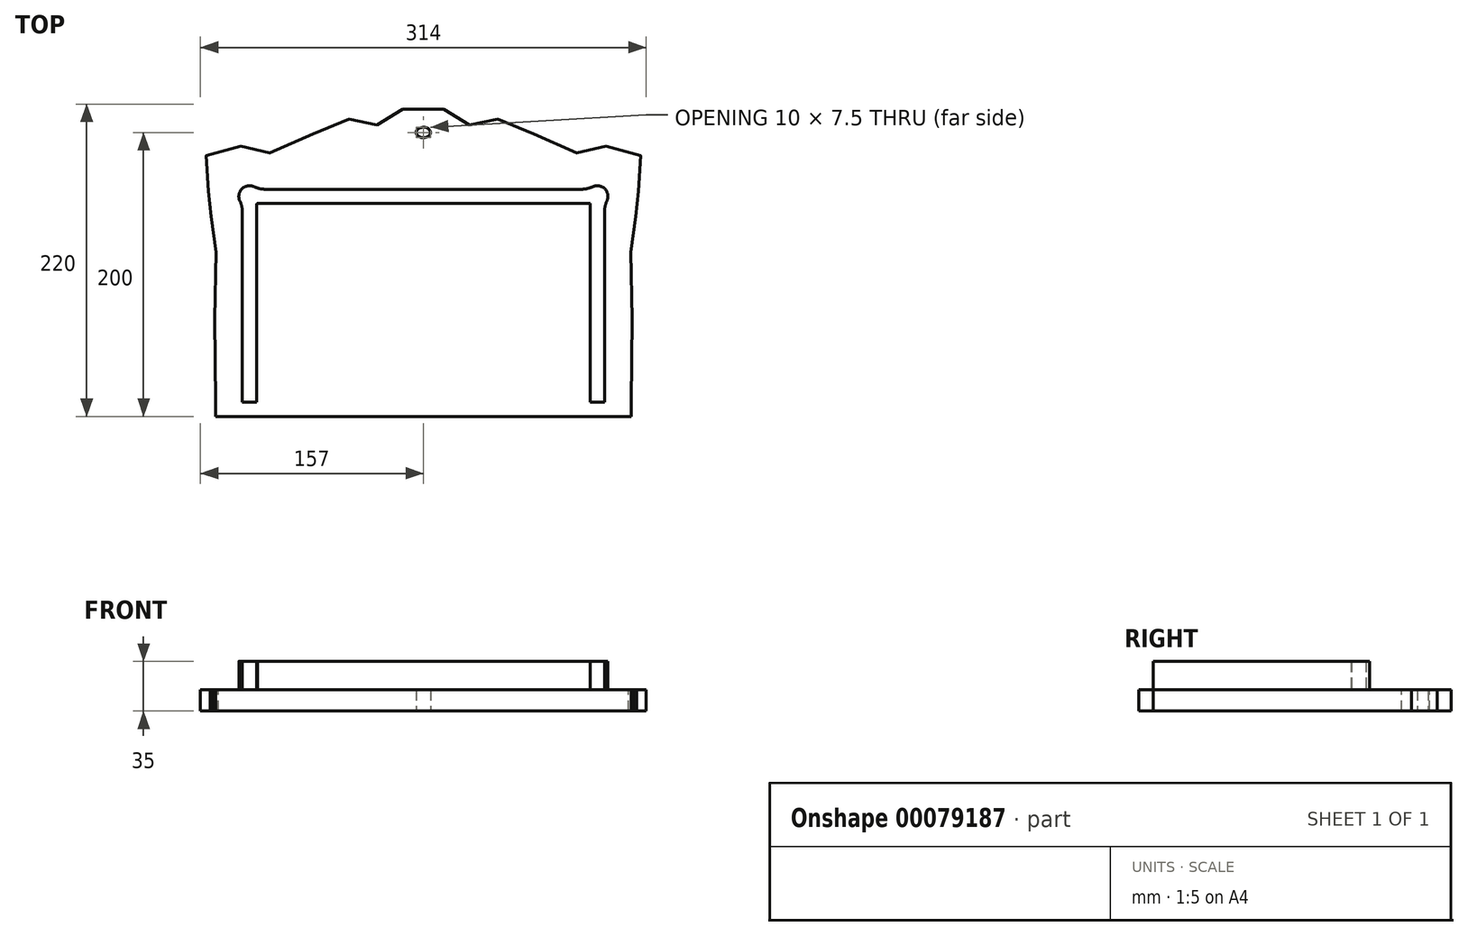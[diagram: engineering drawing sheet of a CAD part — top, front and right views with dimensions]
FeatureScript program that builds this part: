
annotation { "Feature Type Name" : "Feature", "Feature Type Description" : "" }
export const myFeature = defineFeature(function(context is Context, id is Id, definition is map)
    precondition{}
    {
        {
            var Q0;
            Q0=qCreatedBy(makeId("Top.planeOp"),FACE);
            var sketch = newSketch(context, id + "F0", { "sketchPlane" : qUnion([Q0])});
            skPoint(sketch, "E0", {"position": v(151.1, 154.93) * mm});
            skPoint(sketch, "E1", {"position": v(140, 77.47) * mm});
            skPoint(sketch, "E2", {"position": v(146.5, 0) * mm});
            skPoint(sketch, "E3", {"position": v(0, 210) * mm});
            skPoint(sketch, "E4", {"position": v(72.86, 179.48) * mm});
            skPoint(sketch, "E5", {"position": v(-38.35, 186.04) * mm});
            skPoint(sketch, "E6", {"position": v(-24.12, 200) * mm});
            skPoint(sketch, "E7", {"position": v(-154.5, 163.42) * mm});
            skLineSegment(sketch, "E8", {"start": v(0, 210) * mm, "end": v(0, -300) * mm, "construction": true});
            skPoint(sketch, "E9.MirrorP", {"position": v(-72.86, 179.48) * mm});
            skPoint(sketch, "E10.MirrorP", {"position": v(-151.1, 154.93) * mm});
            skPoint(sketch, "E11.MirrorP", {"position": v(-140, 77.47) * mm});
            skPoint(sketch, "E12.MirrorP", {"position": v(-146.5, 0) * mm});
            skPoint(sketch, "E13", {"position": v(0, 0) * mm});
            skPoint(sketch, "E14.MirrorP", {"position": v(154.5, 163.42) * mm});
            skPoint(sketch, "E15.MirrorP", {"position": v(38.35, 186.04) * mm});
            skPoint(sketch, "E16.MirrorP", {"position": v(24.12, 200) * mm});
            skPoint(sketch, "E17", {"position": v(-111.22, 185.44) * mm});
            skPoint(sketch, "E18.MirrorP", {"position": v(111.21, 185.44) * mm});
            skLineSegment(sketch, "E19", {"start": v(-146.5, 0) * mm, "end": v(146.5, 0) * mm});
            skPoint(sketch, "E20", {"position": v(0, 193.84) * mm});
            skPoint(sketch, "E21", {"position": v(-120.16, 190.34) * mm});
            skPoint(sketch, "E22", {"position": v(-131.3, 192.59) * mm});
            skPoint(sketch, "E23", {"position": v(-143.04, 189.12) * mm});
            skPoint(sketch, "E24", {"position": v(-150.16, 182.65) * mm});
            skPoint(sketch, "E25", {"position": v(-153.61, 176.08) * mm});
            skPoint(sketch, "E26", {"position": v(-154.92, 169.2) * mm});
            skPoint(sketch, "E27.MirrorP", {"position": v(120.16, 190.34) * mm});
            skPoint(sketch, "E28.MirrorP", {"position": v(131.3, 192.59) * mm});
            skPoint(sketch, "E29.MirrorP", {"position": v(143.04, 189.12) * mm});
            skPoint(sketch, "E30.MirrorP", {"position": v(150.16, 182.65) * mm});
            skPoint(sketch, "E31.MirrorP", {"position": v(153.61, 176.08) * mm});
            skPoint(sketch, "E32.MirrorP", {"position": v(154.92, 169.2) * mm});
            skFitSpline(sketch, "E33", {"points": [v(-146.5, 0) * mm, v(-140, 77.47) * mm, v(-151.1, 154.93) * mm, v(-154.5, 163.42) * mm, v(-154.92, 169.2) * mm, v(-153.61, 176.08) * mm, v(-150.16, 182.65) * mm, v(-143.04, 189.12) * mm, v(-131.3, 192.59) * mm, v(-120.16, 190.34) * mm, v(-111.22, 185.44) * mm, v(-72.87, 179.48) * mm, v(-38.35, 186.04) * mm, v(-24.12, 200) * mm, v(0, 210) * mm, v(24.12, 200) * mm, v(38.35, 186.04) * mm, v(72.86, 179.48) * mm, v(111.21, 185.44) * mm, v(120.16, 190.34) * mm, v(131.3, 192.59) * mm, v(143.04, 189.12) * mm, v(150.16, 182.65) * mm, v(153.61, 176.08) * mm, v(154.92, 169.2) * mm, v(154.5, 163.42) * mm, v(151.1, 154.93) * mm, v(140, 77.47) * mm, v(146.5, 0) * mm], "startDerivative": vector(163.85, 1049.48) * mm, "endDerivative": vector(163.85, -1049.48) * mm});
            skLineSegment(sketch, "E34.bottom", {"start": v(-107.5, 0) * mm, "end": v(107.5, 0) * mm});
            skSolve(sketch);
        }
        {
            var Q0;
            Q0=qCreatedBy(makeId("Top.planeOp"),FACE);
            cPlane(context, id + "F1", {"entities" : qUnion([Q0]), "cplaneType" : CPlaneType.OFFSET, "offset" : 100 * mm, "width" : 150 * mm, "height" : 150 * mm});
        }
        {
            var Q0;
            Q0=qCreatedBy(id+"F1.planeOp",FACE);
            var sketch = newSketch(context, id + "F2", { "sketchPlane" : qUnion([Q0])});
            skPoint(sketch, "E35.0", {"position": v(-146.5, 0) * mm});
            skPoint(sketch, "E36", {"position": v(-150, 128) * mm});
            skPoint(sketch, "E37", {"position": v(-15, 206) * mm});
            skPoint(sketch, "E38", {"position": v(-83.69, 186) * mm});
            skPoint(sketch, "E39", {"position": v(-57.22, 198) * mm});
            skPoint(sketch, "E40.16.internal.orphan", {"position": v(-102.04, 177) * mm});
            skPoint(sketch, "E40.2.internal.orphan", {"position": v(-147, 60) * mm});
            skLineSegment(sketch, "E41", {"start": v(-146.5, 0) * mm, "end": v(146.5, 0) * mm});
            skLineSegment(sketch, "E42", {"start": v(0, 0) * mm, "end": v(0, 210) * mm, "construction": true});
            skPoint(sketch, "E42.endSnap0", {"position": v(0, 0) * mm});
            skLineSegment(sketch, "E43", {"start": v(214.08, 0) * mm, "end": v(-299.05, 0) * mm, "construction": true});
            skPoint(sketch, "E44.10.internal.orphan", {"position": v(-151, 176) * mm});
            skPoint(sketch, "E44.11.internal.orphan", {"position": v(-138, 182) * mm});
            skPoint(sketch, "E44.12.internal.orphan", {"position": v(-116, 175) * mm});
            skPoint(sketch, "E44.15.internal.orphan", {"position": v(-67.88, 193.66) * mm});
            skPoint(sketch, "E44.17.internal.orphan", {"position": v(-46.27, 200) * mm});
            skPoint(sketch, "E44.18.internal.orphan", {"position": v(-38.42, 198) * mm});
            skPoint(sketch, "E44.19.internal.orphan", {"position": v(-34.04, 196) * mm});
            skPoint(sketch, "E44.2.internal.orphan", {"position": v(-145, 100) * mm});
            skPoint(sketch, "E44.20.internal.orphan", {"position": v(-29, 195) * mm});
            skPoint(sketch, "E44.21.internal.orphan", {"position": v(-25, 198) * mm});
            skPoint(sketch, "E44.3.internal.orphan", {"position": v(-150, 121) * mm});
            skPoint(sketch, "E44.5.internal.orphan", {"position": v(-149, 133) * mm});
            skPoint(sketch, "E44.6.internal.orphan", {"position": v(-147.5, 139) * mm});
            skPoint(sketch, "E44.7.internal.orphan", {"position": v(-149, 145) * mm});
            skPoint(sketch, "E44.8.internal.orphan", {"position": v(-153, 151) * mm});
            skPoint(sketch, "E44.9.internal.orphan", {"position": v(-157, 163) * mm});
            skPoint(sketch, "E45.MirrorP", {"position": v(15, 206) * mm});
            skPoint(sketch, "E46.MirrorP", {"position": v(29, 195) * mm});
            skPoint(sketch, "E47.MirrorP", {"position": v(102.04, 177) * mm});
            skPoint(sketch, "E48.MirrorP", {"position": v(83.69, 186) * mm});
            skPoint(sketch, "E49.MirrorP", {"position": v(46.27, 200) * mm});
            skPoint(sketch, "E50.MirrorP", {"position": v(25, 198) * mm});
            skPoint(sketch, "E51.MirrorP", {"position": v(149, 133) * mm});
            skPoint(sketch, "E52.MirrorP", {"position": v(151, 176) * mm});
            skPoint(sketch, "E53.MirrorP", {"position": v(149, 145) * mm});
            skPoint(sketch, "E54.MirrorP", {"position": v(147, 60) * mm});
            skPoint(sketch, "E55.MirrorP", {"position": v(150, 128) * mm});
            skPoint(sketch, "E56.MirrorP", {"position": v(145, 100) * mm});
            skPoint(sketch, "E57.MirrorP", {"position": v(38.42, 198) * mm});
            skPoint(sketch, "E58.MirrorP", {"position": v(67.88, 193.66) * mm});
            skPoint(sketch, "E59.MirrorP", {"position": v(153, 151) * mm});
            skPoint(sketch, "E60.MirrorP", {"position": v(150, 121) * mm});
            skPoint(sketch, "E61.MirrorP", {"position": v(57.22, 198) * mm});
            skPoint(sketch, "E62.MirrorP", {"position": v(116, 175) * mm});
            skPoint(sketch, "E63.MirrorP", {"position": v(138, 182) * mm});
            skPoint(sketch, "E64.MirrorP", {"position": v(147.5, 139) * mm});
            skPoint(sketch, "E65.MirrorP", {"position": v(157, 163) * mm});
            skPoint(sketch, "E66.MirrorP", {"position": v(34.04, 196) * mm});
            skPoint(sketch, "E67", {"position": v(-123.4, 176.5) * mm});
            skPoint(sketch, "E68", {"position": v(-128, 180) * mm});
            skPoint(sketch, "E69.MirrorP", {"position": v(123.4, 176.5) * mm});
            skPoint(sketch, "E70.MirrorP", {"position": v(128, 180) * mm});
            skFitSpline(sketch, "E71", {"points": [v(-146.5, 0) * mm, v(-147, 60) * mm, v(-145, 100) * mm, v(-150, 121) * mm, v(-150, 128) * mm, v(-149, 133) * mm, v(-147.5, 139) * mm, v(-149, 145) * mm, v(-153, 151) * mm, v(-157, 163) * mm, v(-151, 176) * mm, v(-138, 182) * mm, v(-128, 180) * mm, v(-123.4, 176.5) * mm, v(-116, 175) * mm, v(-102.04, 177) * mm, v(-83.69, 186) * mm, v(-67.88, 193.66) * mm, v(-57.22, 198) * mm, v(-46.27, 200) * mm, v(-38.42, 198) * mm, v(-34.04, 196) * mm, v(-29, 195) * mm, v(-25, 198) * mm, v(-15, 206) * mm, v(0, 210) * mm, v(15, 206) * mm, v(25, 198) * mm, v(29, 195) * mm, v(34.04, 196) * mm, v(38.42, 198) * mm, v(46.27, 200) * mm, v(57.22, 198) * mm, v(67.88, 193.66) * mm, v(83.69, 186) * mm, v(102.04, 177) * mm, v(116, 175) * mm, v(123.4, 176.5) * mm, v(128, 180) * mm, v(138, 182) * mm, v(151, 176) * mm, v(157, 163) * mm, v(153, 151) * mm, v(149, 145) * mm, v(147.5, 139) * mm, v(149, 133) * mm, v(150, 128) * mm, v(150, 121) * mm, v(145, 100) * mm, v(147, 60) * mm, v(146.5, 0) * mm], "startDerivative": vector(-209.03, 1625.36) * mm, "endDerivative": vector(-209.03, -1625.36) * mm});
            skEllipse(sketch, "E72", {"center": v(0, 190) * mm, "majorRadius": 5 * mm, "minorRadius": 3.75 * mm, "majorAxis": v(1, 0)});
            skLineSegment(sketch, "E73.top", {"start": v(-146.5, -10) * mm, "end": v(146.5, -10) * mm});
            skLineSegment(sketch, "E73.left", {"start": v(-146.5, 0) * mm, "end": v(-146.5, -10) * mm});
            skLineSegment(sketch, "E73.right", {"start": v(146.5, 0) * mm, "end": v(146.5, -10) * mm});
            skSolve(sketch);
        }
        {
            var Q0;
            Q0=makeQuery(id+"F2.imprint","IMPRINT",FACE,{"disambiguationData":[TD([[makeQuery(id+"F2.imprint","IMPRINT",EDGE,{"derivedFrom":sQuery(id+"F2.wireOp",EDGE,"E41")}),1.0]])]});
            var Q1;
            Q1=makeQuery(id+"F2.imprint","IMPRINT",FACE,{"disambiguationData":[TD([[makeQuery(id+"F2.imprint","IMPRINT",EDGE,{"derivedFrom":sQuery(id+"F2.wireOp",EDGE,"E71")}),-1.0]])]});
            var Q2;
            Q2=makeQuery(id+"F2.imprint","IMPRINT",FACE,{"disambiguationData":[TD([[makeQuery(id+"F2.imprint","IMPRINT",EDGE,{"derivedFrom":sQuery(id+"F2.wireOp",EDGE,"E41")}),-1.0]])]});
            extrude(context, id + "F3", {"entities" : qUnion([Q0, Q1, Q2]), "depth" : 15 * mm, "offsetDistance" : 25 * mm});
        }
        {
            var Q0;
            Q0=makeQuery(id+"F3.opExtrude","CAP_FACE",FACE,{"disambiguationData":[OSD([sQuery(id+"F2.wireOp",EDGE,"E41"),sQuery(id+"F2.wireOp",EDGE,"E71")])],"isStart":false});
            var sketch = newSketch(context, id + "F4", { "sketchPlane" : qUnion([Q0])});
            skLineSegment(sketch, "E74.bottom", {"start": v(-127.5, 0) * mm, "end": v(127.5, 0) * mm});
            skLineSegment(sketch, "E74.top", {"start": v(-127.5, 150) * mm, "end": v(127.5, 150) * mm});
            skLineSegment(sketch, "E74.left", {"start": v(-127.5, 0) * mm, "end": v(-127.5, 150) * mm});
            skLineSegment(sketch, "E74.right", {"start": v(127.5, 0) * mm, "end": v(127.5, 150) * mm});
            skLineSegment(sketch, "E75.bottom", {"start": v(-117.5, 0) * mm, "end": v(117.5, 0) * mm});
            skLineSegment(sketch, "E75.top", {"start": v(-117.5, 140) * mm, "end": v(117.5, 140) * mm});
            skLineSegment(sketch, "E75.left", {"start": v(-117.5, 0) * mm, "end": v(-117.5, 140) * mm});
            skLineSegment(sketch, "E75.right", {"start": v(117.5, 0) * mm, "end": v(117.5, 140) * mm});
            skLineSegment(sketch, "E76", {"start": v(-127.5, 150) * mm, "end": v(-117.5, 140) * mm});
            skCircle(sketch, "E77", {"center": v(-122.5, 145) * mm, "radius": 7.5 * mm});
            skCircle(sketch, "E78.MirrorC", {"center": v(122.5, 145) * mm, "radius": 7.5 * mm});
            skSolve(sketch);
        }
        {
            var Q0;
            Q0=makeQuery(id+"F4.imprint","IMPRINT",FACE,{"disambiguationData":[TD([[makeQuery(id+"F4.imprint","IMPRINT",EDGE,{"derivedFrom":sQuery(id+"F4.wireOp",EDGE,"E74.top")}),-1.0]])]});
            var Q1;
            Q1=makeQuery(id+"F4.imprint","IMPRINT",FACE,{"disambiguationData":[TD([[makeQuery(id+"F4.imprint","IMPRINT",EDGE,{"derivedFrom":sQuery(id+"F4.wireOp",EDGE,"E75.bottom")}),1.0]])]});
            var Q2;
            {var subQ0=sQuery(id+"F4.wireOp",EDGE,"E76");Q2=makeQuery(id+"F4.imprint","IMPRINT",FACE,{"disambiguationData":[TD([[makeQuery(id+"F4.imprint","IMPRINT",EDGE,{"derivedFrom":subQ0}),-1.0]])]});}
            var Q3;
            {var subQ1=sQuery(id+"F4.wireOp",EDGE,"E75.top");var subQ3=sQuery(id+"F4.wireOp",EDGE,"E77");var subQ4=makeQuery(id+"F4.imprint","INTERSECT",VERTEX,{"derivedFrom":[subQ1,subQ3]});Q3=makeQuery(id+"F4.imprint","IMPRINT",FACE,{"disambiguationData":[TD([[makeQuery(id+"F4.imprint","IMPRINT",EDGE,{"disambiguationData":[TD([[subQ4,1.0]])],"derivedFrom":subQ3}),1.0]])]});}
            var Q4;
            {var subQ0=sQuery(id+"F4.wireOp",EDGE,"E74.left");var subQ5=sQuery(id+"F4.wireOp",EDGE,"E77");var subQ7=makeQuery(id+"F4.imprint","INTERSECT",VERTEX,{"derivedFrom":[subQ0,subQ5]});Q4=makeQuery(id+"F4.imprint","IMPRINT",FACE,{"disambiguationData":[TD([[makeQuery(id+"F4.imprint","IMPRINT",EDGE,{"disambiguationData":[TD([[subQ7,-1.0]])],"derivedFrom":subQ5}),-1.0]])]});}
            var Q5;
            {var subQ4=sQuery(id+"F4.wireOp",EDGE,"E74.right");Q5=makeQuery(id+"F4.imprint","IMPRINT",FACE,{"disambiguationData":[TD([[makeQuery(id+"F4.imprint","IMPRINT",EDGE,{"derivedFrom":subQ4}),1.0]])]});}
            var Q6;
            {var subQ1=sQuery(id+"F4.wireOp",EDGE,"E74.top");var subQ3=sQuery(id+"F4.wireOp",EDGE,"E77");var subQ4=makeQuery(id+"F4.imprint","INTERSECT",VERTEX,{"derivedFrom":[subQ1,subQ3]});Q6=makeQuery(id+"F4.imprint","IMPRINT",FACE,{"disambiguationData":[TD([[makeQuery(id+"F4.imprint","IMPRINT",EDGE,{"disambiguationData":[TD([[subQ4,-1.0]])],"derivedFrom":subQ3}),1.0]])]});}
            var Q7;
            {var subQ6=sQuery(id+"F4.wireOp",EDGE,"E74.right");var subQ8=sQuery(id+"F4.wireOp",EDGE,"E74.top");var subQ9=makeQuery(id+"F4.imprint","INTERSECT",VERTEX,{"derivedFrom":[subQ8,subQ6]});Q7=makeQuery(id+"F4.imprint","IMPRINT",FACE,{"disambiguationData":[TD([[makeQuery(id+"F4.imprint","IMPRINT",EDGE,{"disambiguationData":[TD([[subQ9,1.0]])],"derivedFrom":subQ8}),-1.0]])]});}
            var Q8;
            {var subQ0=sQuery(id+"F4.wireOp",EDGE,"E74.right");var subQ1=sQuery(id+"F4.wireOp",EDGE,"E74.top");var subQ2=makeQuery(id+"F4.imprint","INTERSECT",VERTEX,{"derivedFrom":[subQ1,subQ0]});Q8=makeQuery(id+"F4.imprint","IMPRINT",FACE,{"disambiguationData":[TD([[makeQuery(id+"F4.imprint","IMPRINT",EDGE,{"disambiguationData":[TD([[subQ2,1.0]])],"derivedFrom":subQ1}),1.0]])]});}
            extrude(context, id + "F5", {"entities" : qUnion([Q0, Q1, Q2, Q3, Q4, Q5, Q6, Q7, Q8]), "depth" : 10 * mm, "offsetDistance" : 25 * mm});
        }
        {
            var Q0;
            Q0=makeQuery(id+"F5.opExtrude","SWEPT_EDGE",EDGE,{"disambiguationData":[OSD([sQuery(id+"F4.wireOp",EDGE,"E74.top"),sQuery(id+"F4.wireOp",EDGE,"E77")])]});
            var Q1;
            Q1=makeQuery(id+"F5.opExtrude","SWEPT_EDGE",EDGE,{"disambiguationData":[OSD([sQuery(id+"F4.wireOp",EDGE,"E74.left"),sQuery(id+"F4.wireOp",EDGE,"E77")])]});
            var Q2;
            Q2=makeQuery(id+"F5.opExtrude","SWEPT_EDGE",EDGE,{"disambiguationData":[OSD([sQuery(id+"F4.wireOp",EDGE,"E74.top"),sQuery(id+"F4.wireOp",EDGE,"E78.MirrorC")])]});
            var Q3;
            Q3=makeQuery(id+"F5.opExtrude","SWEPT_EDGE",EDGE,{"disambiguationData":[OSD([sQuery(id+"F4.wireOp",EDGE,"E74.right"),sQuery(id+"F4.wireOp",EDGE,"E78.MirrorC")])]});
            fillet(context, id + "F6", {"entities" : qUnion([Q0, Q1, Q2, Q3]), "radius" : 20 * mm, "tangentPropagation" : true, "allowEdgeOverflow" : false});
        }
        {
            var Q0;
            Q0=makeQuery(id+"F5.opExtrude","CAP_FACE",FACE,{"disambiguationData":[OSD([sQuery(id+"F01OqzFfX9itPD7_1.wireOp",EDGE,"TDFwYFJC-9rLf-SEpr-LMun-f7n9ZEvJ4hNh"),sQuery(id+"F01OqzFfX9itPD7_1.wireOp",EDGE,"fCgicrGS-55NG-sWUy-wnvS-e9e9rh1w3ghR"),sQuery(id+"F01OqzFfX9itPD7_1.wireOp",EDGE,"5ItRyK9n-nWWQ-e84D-iQgI-aiFtkuca7bxh"),sQuery(id+"F4.wireOp",EDGE,"E74.bottom"),sQuery(id+"F4.wireOp",EDGE,"E74.top"),sQuery(id+"F4.wireOp",EDGE,"E74.left"),sQuery(id+"F4.wireOp",EDGE,"E74.right"),sQuery(id+"F4.wireOp",EDGE,"E75.bottom")])],"isStart":false});
            var sketch = newSketch(context, id + "F7", { "sketchPlane" : qUnion([Q0])});
            skLineSegment(sketch, "E79.0", {"start": v(117.5, 0) * mm, "end": v(117.5, 140) * mm});
            skLineSegment(sketch, "E80.0", {"start": v(-117.5, 140) * mm, "end": v(117.5, 140) * mm});
            skLineSegment(sketch, "E81.0", {"start": v(-117.5, 0) * mm, "end": v(-117.5, 140) * mm});
            skLineSegment(sketch, "E82.0", {"start": v(-117.5, 0) * mm, "end": v(117.5, 0) * mm});
            skPoint(sketch, "E83.orphan", {"position": v(-117.5, 140) * mm});
            skSolve(sketch);
        }
        {
            var Q0;
            {var subQ0=sQuery(id+"F7.wireOp",EDGE,"E81.0");Q0=makeQuery(id+"F7.imprint","IMPRINT",FACE,{"disambiguationData":[TD([[makeQuery(id+"F7.imprint","IMPRINT",EDGE,{"derivedFrom":subQ0}),-1.0]])]});}
            var Q1;
            {var subQ0=sQuery(id+"F7.wireOp",EDGE,"eHPwFbGt-x49O-upP5-2J7X-MqRqS1DIb1iX");var subQ1=makeQuery(id+"F7.imprint","INTERSECT",VERTEX,{"derivedFrom":[sQuery(id+"F7.wireOp",EDGE,"E80.0"),subQ0]});Q1=makeQuery(id+"F7.imprint","IMPRINT",FACE,{"disambiguationData":[TD([[makeQuery(id+"F7.imprint","IMPRINT",EDGE,{"disambiguationData":[TD([[subQ1,-1.0]])],"derivedFrom":subQ0}),1.0]])]});}
            var Q2;
            {var subQ1=sQuery(id+"F7.wireOp",EDGE,"E79.0");var subQ6=sQuery(id+"F7.wireOp",EDGE,"a167e5de-4d74-4f45-bc02-d425cc1066e10.MirrorC");var subQ9=makeQuery(id+"F7.imprint","INTERSECT",VERTEX,{"derivedFrom":[subQ1,subQ6]});Q2=makeQuery(id+"F7.imprint","IMPRINT",FACE,{"disambiguationData":[TD([[makeQuery(id+"F7.imprint","IMPRINT",EDGE,{"disambiguationData":[TD([[subQ9,1.0]])],"derivedFrom":subQ6}),-1.0]])]});}
            var Q3;
            {var subQ1=sQuery(id+"F4.wireOp",EDGE,"E78.MirrorC");var subQ2=makeQuery(id+"F5.opExtrude","CAP_EDGE",EDGE,{"disambiguationData":[OSD([subQ1]),TDD([makeQuery(id+"F4.imprint","IMPRINT",EDGE,{"disambiguationData":[TD([[makeQuery(id+"F4.imprint","INTERSECT",VERTEX,{"derivedFrom":[sQuery(id+"F4.wireOp",EDGE,"E75.top"),subQ1]}),1.0]])],"derivedFrom":subQ1})])],"isStart":false});Q3=makeQuery(id+"F7.imprint","IMPRINT",FACE,{"disambiguationData":[TD([[makeQuery(id+"F7.imprint","IMPRINT",EDGE,{"derivedFrom":subQ2}),1.0]])]});}
            var Q4;
            {var subQ0=sQuery(id+"F7.wireOp",EDGE,"c7arcQw8-U9WH-50iv-UKyZ-HqhImG9bkcTv");var subQ1=makeQuery(id+"F7.imprint","INTERSECT",VERTEX,{"derivedFrom":[sQuery(id+"F7.wireOp",EDGE,"E80.0"),subQ0]});Q4=makeQuery(id+"F7.imprint","IMPRINT",FACE,{"disambiguationData":[TD([[makeQuery(id+"F7.imprint","IMPRINT",EDGE,{"disambiguationData":[TD([[subQ1,-1.0]])],"derivedFrom":subQ0}),1.0]])]});}
            var Q5;
            {var subQ1=sQuery(id+"F7.wireOp",EDGE,"E79.0");var subQ6=sQuery(id+"F7.wireOp",EDGE,"c4ad2870-bfd3-4a91-94f6-d68b5c8148240.MirrorC");var subQ9=makeQuery(id+"F7.imprint","INTERSECT",VERTEX,{"derivedFrom":[subQ1,subQ6]});Q5=makeQuery(id+"F7.imprint","IMPRINT",FACE,{"disambiguationData":[TD([[makeQuery(id+"F7.imprint","IMPRINT",EDGE,{"disambiguationData":[TD([[subQ9,1.0]])],"derivedFrom":subQ6}),-1.0]])]});}
            extrude(context, id + "F8", {"entities" : qUnion([Q0, Q1, Q2, Q3, Q4, Q5]), "operationType" : NewBodyOperationType.ADD, "depth" : 10 * mm, "offsetDistance" : 25 * mm});
        }
        {
            var Q0;
            Q0=makeQuery(id+"F8.opExtrude","CAP_FACE",FACE,{"disambiguationData":[OSD([sQuery(id+"F4.wireOp",EDGE,"E78.MirrorC"),sQuery(id+"F7.wireOp",EDGE,"E79.0"),sQuery(id+"F7.wireOp",EDGE,"E80.0"),sQuery(id+"F7.wireOp",EDGE,"E81.0"),sQuery(id+"F7.wireOp",EDGE,"E82.0")])],"isStart":false});
            var sketch = newSketch(context, id + "F9", { "sketchPlane" : qUnion([Q0])});
            skLineSegment(sketch, "E84", {"start": v(-107.5, 0) * mm, "end": v(-107.5, 130) * mm});
            skLineSegment(sketch, "E85", {"start": v(-107.5, 130) * mm, "end": v(107.5, 130) * mm});
            skLineSegment(sketch, "E86", {"start": v(107.5, 130) * mm, "end": v(107.5, 0) * mm});
            skLineSegment(sketch, "E87", {"start": v(107.5, 0) * mm, "end": v(-107.5, 0) * mm});
            skSolve(sketch);
        }
        {
            var Q0;
            Q0=makeQuery(id+"F9.imprint","IMPRINT",FACE,{"disambiguationData":[TD([[makeQuery(id+"F9.imprint","IMPRINT",EDGE,{"derivedFrom":sQuery(id+"F9.wireOp",EDGE,"E84")}),-1.0]])]});
            extrude(context, id + "F10", {"entities" : qUnion([Q0]), "operationType" : NewBodyOperationType.REMOVE, "oppositeDirection" : true, "depth" : 10 * mm, "offsetDistance" : 25 * mm});
        }
        {
            var Q0;
            {var subQ10=sQuery(id+"F7.wireOp",EDGE,"E81.0");Q0=makeQuery(id+"F7.imprint","IMPRINT",FACE,{"disambiguationData":[TD([[makeQuery(id+"F7.imprint","IMPRINT",EDGE,{"derivedFrom":subQ10}),1.0]])]});}
            extrude(context, id + "F11", {"entities" : qUnion([Q0]), "operationType" : NewBodyOperationType.ADD, "depth" : 10 * mm, "offsetDistance" : 25 * mm});
        }
    });
